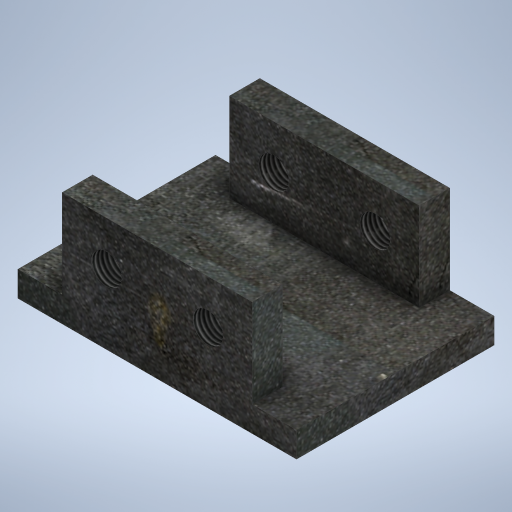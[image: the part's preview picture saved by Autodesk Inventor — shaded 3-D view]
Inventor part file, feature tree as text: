
AUTODESK INVENTOR PART (.ipt)
format: ipt  version: 2024 (Build 280153000, 153)  size: 489,984 bytes
history: native  units: mm
features: thread x4, extrude x3, sketch x3, mirror x1
ambient origin geometry x8: Origin, YZ Plane, XZ Plane, XY Plane, X Axis, Y Axis, Z Axis, Center Point
bodies: Solid1 (feature_tree)
feature tree (11):
  extrude  "Extrusion1"  Depth=110.0mm
  extrude  "Extrusion2"  Depth=39.0mm
  sketch  "Sketch3"  dims[d4=10.0mm d5=0.0mm d6=12.0mm d8=37.5mm d9=75.0mm d10=35.0mm d11=0.0mm d14=33.0mm d16=12.0mm d17=12.0mm d18=27.5mm d19=27.5mm d20=40.0mm d21=20.0mm d24=80.0mm d25=0.0mm d42=350.0mm d43=0.0mm d50=600.0mm d51=0.0mm d52=600.0mm d53=0.0mm d54=600.0mm d55=0.0mm d34=0.5mm d35=0.872665mm d36=0.5mm d37=0.872665mm]
  extrude  "Extrusion3"  Depth=12.0mm
  mirror  "Mirror1"
  thread  "Thread9"  [1 undecoded]
  thread  "Thread13"  [1 undecoded]
  thread  "Thread14"  [1 undecoded]
  thread  "Thread15"  [1 undecoded]
  sketch  "Sketch1"  dims[d0=78.0mm d1=110.0mm]
  sketch  "Sketch2"  dims[d2=55.0mm d3=39.0mm]
note: 4 required parameter values undecoded (feature->parameter linkage not recoverable at this tier; creation-order binding heuristic only, values carry confidence <= 0.55)
